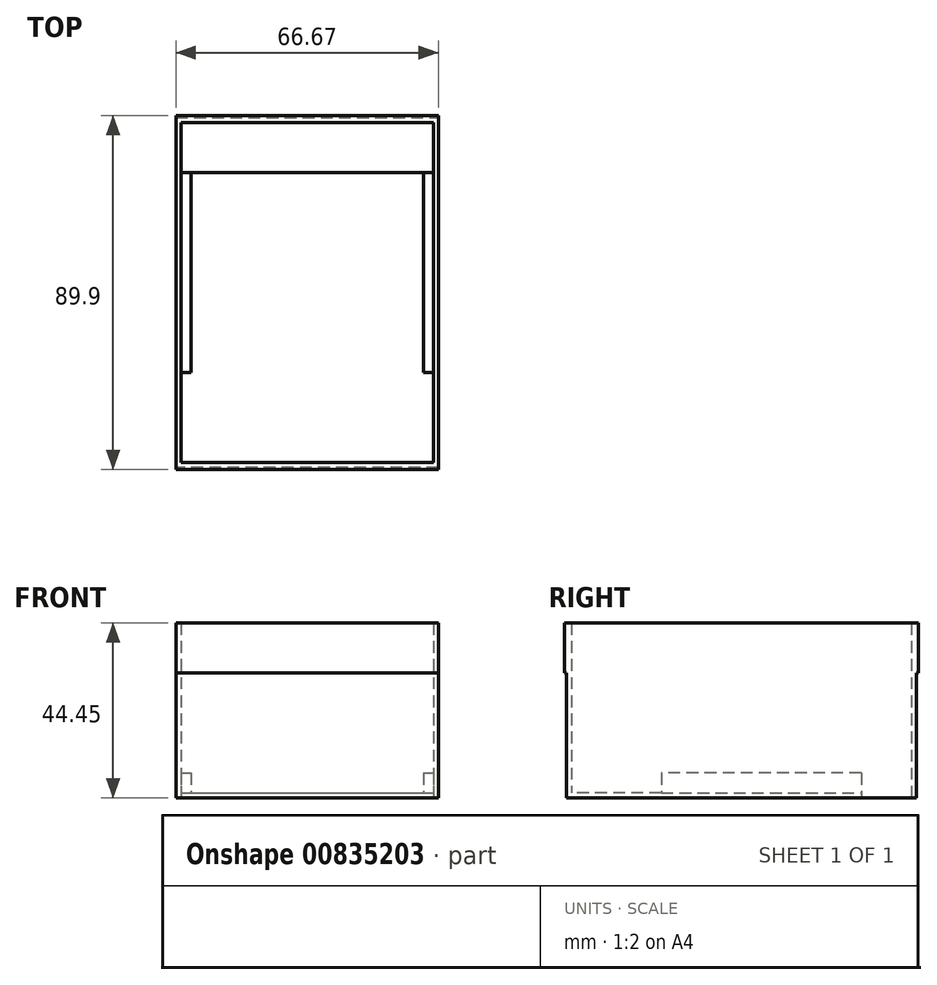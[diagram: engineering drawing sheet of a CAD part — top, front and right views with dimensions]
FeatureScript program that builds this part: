
annotation { "Feature Type Name" : "Feature", "Feature Type Description" : "" }
export const myFeature = defineFeature(function(context is Context, id is Id, definition is map)
    precondition{}
    {
        {
            var Q0;
            Q0=qCreatedBy(makeId("Top.planeOp"),FACE);
            var sketch = newSketch(context, id + "F0", { "sketchPlane" : qUnion([Q0])});
            skLineSegment(sketch, "E0.bottom", {"start": v(-34.46, 55.3) * mm, "end": v(32.21, 55.3) * mm});
            skLineSegment(sketch, "E0.top", {"start": v(-34.46, -33.6) * mm, "end": v(32.21, -33.6) * mm});
            skLineSegment(sketch, "E0.left", {"start": v(-34.46, 55.3) * mm, "end": v(-34.46, -33.6) * mm});
            skLineSegment(sketch, "E0.right", {"start": v(32.21, 55.3) * mm, "end": v(32.21, -33.6) * mm});
            skSolve(sketch);
        }
        {
            var Q0;
            Q0=makeQuery(id+"F0.imprint","IMPRINT",FACE,{"disambiguationData":[TD([[makeQuery(id+"F0.imprint","IMPRINT",EDGE,{"derivedFrom":sQuery(id+"F0.wireOp",EDGE,"E0.bottom")}),-1.0]])]});
            extrude(context, id + "F1", {"entities" : qUnion([Q0]), "depth" : 44.45 * mm, "offsetDistance" : 25.4 * mm});
        }
        {
            var Q0;
            Q0=makeQuery(id+"F1.opExtrude","CAP_FACE",FACE,{"disambiguationData":[OSD([sQuery(id+"F0.wireOp",EDGE,"E0.bottom"),sQuery(id+"F0.wireOp",EDGE,"E0.top"),sQuery(id+"F0.wireOp",EDGE,"E0.left"),sQuery(id+"F0.wireOp",EDGE,"E0.right")])],"isStart":false});
            shell(context, id + "F2", {"entities" : qUnion([Q0]), "thickness" : 1.27 * mm});
        }
        {
            var Q0;
            Q0=makeQuery(id+"F2.opShell","OFFSET_FACE",FACE,{"disambiguationData":[OSD([sQuery(id+"F0.wireOp",EDGE,"E0.bottom"),sQuery(id+"F0.wireOp",EDGE,"E0.top"),sQuery(id+"F0.wireOp",EDGE,"E0.left"),sQuery(id+"F0.wireOp",EDGE,"E0.right")])]});
            var sketch = newSketch(context, id + "F3", { "sketchPlane" : qUnion([Q0])});
            skLineSegment(sketch, "E1", {"start": v(-33.2, 41.34) * mm, "end": v(30.94, 41.34) * mm});
            skLineSegment(sketch, "E2", {"start": v(-33.2, -9.46) * mm, "end": v(30.94, -9.46) * mm});
            skLineSegment(sketch, "E3", {"start": v(28.4, 41.34) * mm, "end": v(28.4, -9.46) * mm});
            skLineSegment(sketch, "E4", {"start": v(-30.65, -9.46) * mm, "end": v(-30.65, 41.34) * mm});
            skLineSegment(sketch, "E5", {"start": v(-30.65, -0.2) * mm, "end": v(28.4, -0.2) * mm});
            skLineSegment(sketch, "E6", {"start": v(-30.65, -3.37) * mm, "end": v(28.4, -3.37) * mm});
            skLineSegment(sketch, "E7.top", {"start": v(-33.2, -22.16) * mm, "end": v(30.94, -22.16) * mm});
            skLineSegment(sketch, "E7.left", {"start": v(-33.2, -9.46) * mm, "end": v(-33.2, -22.16) * mm});
            skLineSegment(sketch, "E7.right", {"start": v(30.94, -9.46) * mm, "end": v(30.94, -22.16) * mm});
            skLineSegment(sketch, "E8.top", {"start": v(-33.2, 54.04) * mm, "end": v(30.94, 54.04) * mm});
            skLineSegment(sketch, "E8.left", {"start": v(-33.2, 41.34) * mm, "end": v(-33.2, 54.04) * mm});
            skLineSegment(sketch, "E8.right", {"start": v(30.94, 41.34) * mm, "end": v(30.94, 54.04) * mm});
            skSolve(sketch);
        }
        {
            var Q0;
            {var subQ4=sQuery(id+"F3.wireOp",EDGE,"E3");Q0=makeQuery(id+"F3.imprint","IMPRINT",FACE,{"disambiguationData":[TD([[makeQuery(id+"F3.imprint","IMPRINT",EDGE,{"derivedFrom":subQ4}),1.0]])]});}
            var Q1;
            {var subQ4=sQuery(id+"F3.wireOp",EDGE,"E4");Q1=makeQuery(id+"F3.imprint","IMPRINT",FACE,{"disambiguationData":[TD([[makeQuery(id+"F3.imprint","IMPRINT",EDGE,{"derivedFrom":subQ4}),1.0]])]});}
            extrude(context, id + "F4", {"entities" : qUnion([Q0, Q1]), "operationType" : NewBodyOperationType.ADD, "depth" : 5.08 * mm, "offsetDistance" : 25.4 * mm});
        }
        {
            var Q0;
            Q0=makeQuery(id+"F1.opExtrude","SWEPT_FACE",FACE,{"disambiguationData":[OSD([sQuery(id+"F0.wireOp",EDGE,"E0.bottom")])]});
            var sketch = newSketch(context, id + "F5", { "sketchPlane" : qUnion([Q0])});
            skLineSegment(sketch, "E9.bottom", {"start": v(34.46, 44.45) * mm, "end": v(-32.21, 44.45) * mm});
            skLineSegment(sketch, "E9.top", {"start": v(34.46, 31.75) * mm, "end": v(-32.21, 31.75) * mm});
            skLineSegment(sketch, "E9.left", {"start": v(34.46, 44.45) * mm, "end": v(34.46, 31.75) * mm});
            skLineSegment(sketch, "E9.right", {"start": v(-32.21, 44.45) * mm, "end": v(-32.21, 31.75) * mm});
            skSolve(sketch);
        }
        {
            var Q0;
            Q0=makeQuery(id+"F5.imprint","IMPRINT",FACE,{"disambiguationData":[TD([[makeQuery(id+"F5.imprint","IMPRINT",EDGE,{"derivedFrom":sQuery(id+"F5.wireOp",EDGE,"E9.bottom")}),1.0]])]});
            extrude(context, id + "F6", {"entities" : qUnion([Q0]), "operationType" : NewBodyOperationType.ADD, "depth" : .5 * mm, "offsetDistance" : 25.4 * mm});
        }
        {
            var Q0;
            Q0=makeQuery(id+"F1.opExtrude","SWEPT_FACE",FACE,{"disambiguationData":[OSD([sQuery(id+"F0.wireOp",EDGE,"E0.top")])]});
            var sketch = newSketch(context, id + "F7", { "sketchPlane" : qUnion([Q0])});
            skLineSegment(sketch, "E10.bottom", {"start": v(32.21, 44.45) * mm, "end": v(-34.46, 44.45) * mm});
            skLineSegment(sketch, "E10.top", {"start": v(32.21, 31.75) * mm, "end": v(-34.46, 31.75) * mm});
            skLineSegment(sketch, "E10.left", {"start": v(32.21, 44.45) * mm, "end": v(32.21, 31.75) * mm});
            skLineSegment(sketch, "E10.right", {"start": v(-34.46, 44.45) * mm, "end": v(-34.46, 31.75) * mm});
            skSolve(sketch);
        }
        {
            var Q0;
            Q0=makeQuery(id+"F7.imprint","IMPRINT",FACE,{"disambiguationData":[TD([[makeQuery(id+"F7.imprint","IMPRINT",EDGE,{"derivedFrom":sQuery(id+"F7.wireOp",EDGE,"E10.bottom")}),-1.0]])]});
            extrude(context, id + "F8", {"entities" : qUnion([Q0]), "operationType" : NewBodyOperationType.ADD, "depth" : .5 * mm, "offsetDistance" : 25.4 * mm});
        }
        {
            var Q0;
            Q0=makeQuery(id+"F3.imprint","IMPRINT",FACE,{"disambiguationData":[TD([[makeQuery(id+"F3.imprint","IMPRINT",EDGE,{"derivedFrom":sQuery(id+"F3.wireOp",EDGE,"E8.top")}),-1.0]])]});
            extrude(context, id + "F9", {"entities" : qUnion([Q0]), "operationType" : NewBodyOperationType.REMOVE, "oppositeDirection" : true, "depth" : 25.4 * mm, "offsetDistance" : 25.4 * mm});
        }
    });
